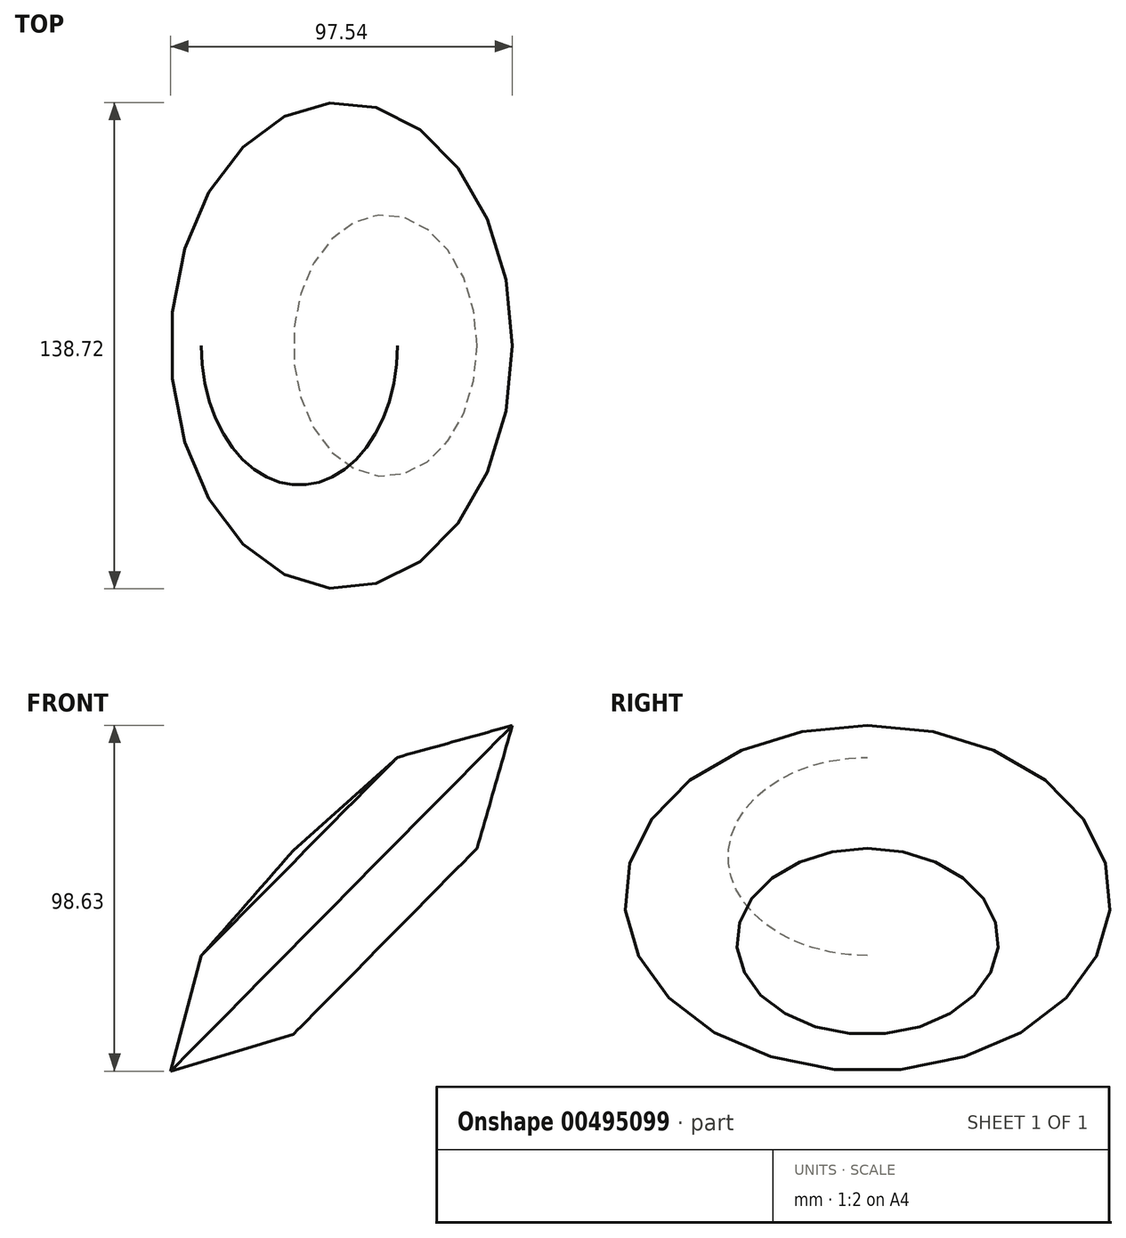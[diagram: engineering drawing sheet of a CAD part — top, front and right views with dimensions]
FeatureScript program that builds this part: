
annotation { "Feature Type Name" : "Feature", "Feature Type Description" : "" }
export const myFeature = defineFeature(function(context is Context, id is Id, definition is map)
    precondition{}
    {
        {
            var Q0;
            Q0=qCreatedBy(makeId("Front.planeOp"),FACE);
            var sketch = newSketch(context, id + "F0", { "sketchPlane" : qUnion([Q0])});
            skLineSegment(sketch, "E0", {"start": v(-38.77, 9.76) * mm, "end": v(-47.51, -23.17) * mm});
            skLineSegment(sketch, "E1", {"start": v(-38.77, 9.76) * mm, "end": v(-12.53, 39.79) * mm});
            skLineSegment(sketch, "E2", {"start": v(-12.53, 39.79) * mm, "end": v(13.7, 13.85) * mm});
            skLineSegment(sketch, "E3", {"start": v(13.7, 13.85) * mm, "end": v(-12.53, -12.68) * mm});
            skLineSegment(sketch, "E4", {"start": v(-12.53, -12.68) * mm, "end": v(-47.51, -23.17) * mm});
            skSolve(sketch);
        }
        {
            var Q0;
            Q0 = qSketchRegion(id + "F0", true);
            var Q1;
            Q1=sQuery(id+"F0.wireOp",EDGE,"E2");
            revolve(context, id + "F1", {"entities" : qUnion([Q0]), "axis" : qUnion([Q1]), "revolveType" : RevolveType.FULL});
        }
    });
